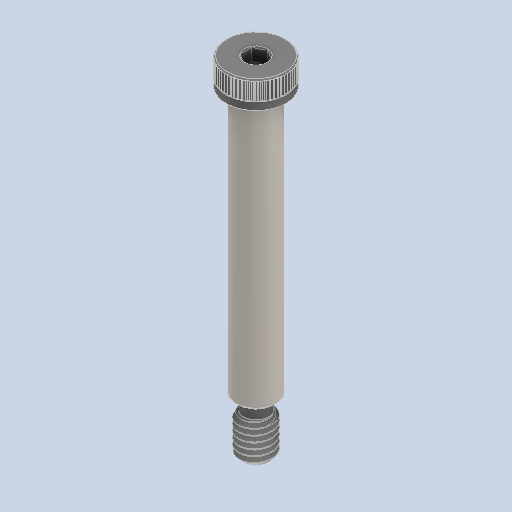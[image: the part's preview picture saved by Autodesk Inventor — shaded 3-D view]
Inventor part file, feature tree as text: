
AUTODESK INVENTOR PART (.ipt)
format: ipt  version: 2024.2 (Build 282272000, 272)  size: 427,520 bytes
history: native  units: in
note: dims shown in document units (in); Inventor stores cm internally (conversion verified against a paired STEP export)
features: chamfer x1
ambient origin geometry x8: Origin, YZ Plane, XZ Plane, XY Plane, X Axis, Y Axis, Z Axis, Center Point
bodies: Solid1 (feature_tree)
feature tree (1):
  chamfer  "Chamfer3"  [1 undecoded]
note: 1 required parameter value undecoded (feature->parameter linkage not recoverable at this tier; creation-order binding heuristic only, values carry confidence <= 0.55)
